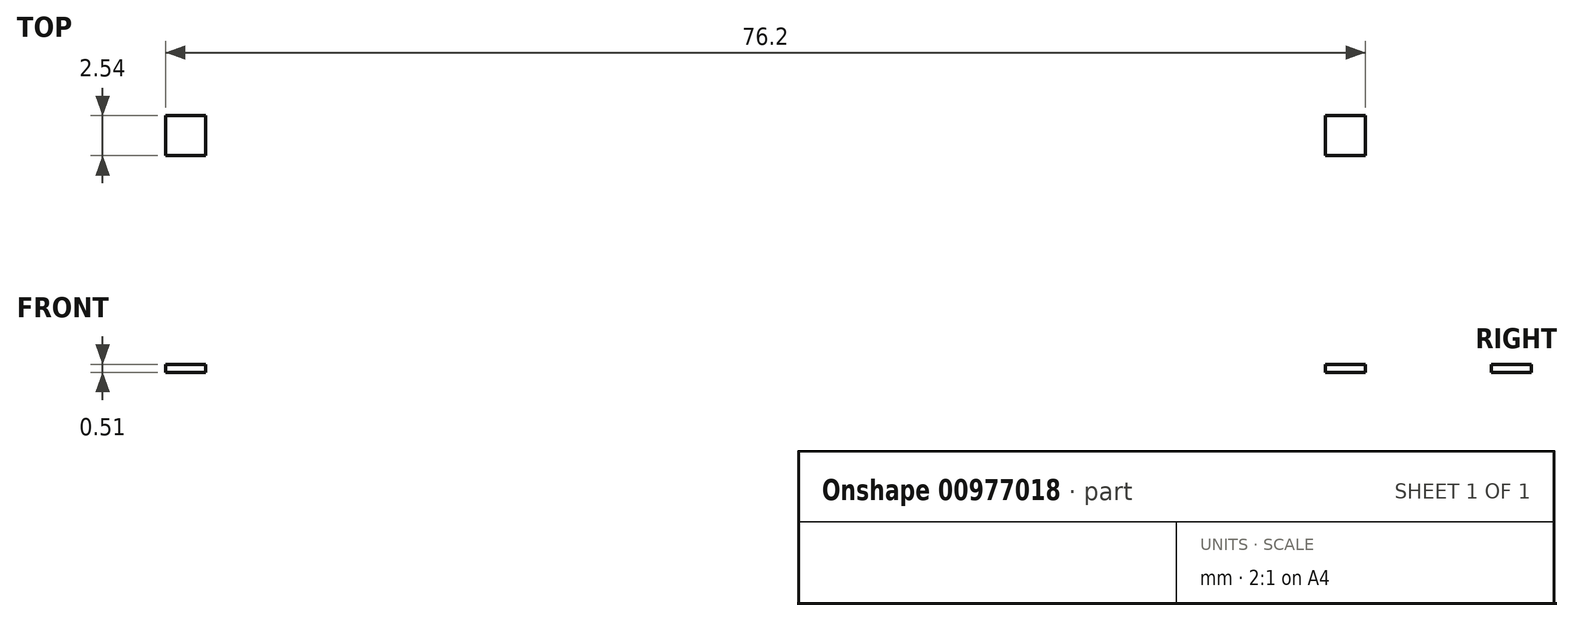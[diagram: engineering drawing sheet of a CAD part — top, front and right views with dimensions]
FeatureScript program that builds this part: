
annotation { "Feature Type Name" : "Feature", "Feature Type Description" : "" }
export const myFeature = defineFeature(function(context is Context, id is Id, definition is map)
    precondition{}
    {
        {
            var Q0;
            Q0=qCreatedBy(makeId("Top.planeOp"),FACE);
            var sketch = newSketch(context, id + "F0", { "sketchPlane" : qUnion([Q0])});
            skLineSegment(sketch, "E0.bottom", {"start": v(0, 0) * mm, "end": v(76.2, 0) * mm});
            skLineSegment(sketch, "E0.top", {"start": v(0, 59.18) * mm, "end": v(76.2, 59.18) * mm});
            skLineSegment(sketch, "E0.left", {"start": v(0, 0) * mm, "end": v(0, 59.18) * mm});
            skLineSegment(sketch, "E0.right", {"start": v(76.2, 0) * mm, "end": v(76.2, 59.18) * mm});
            skLineSegment(sketch, "E1.bottom", {"start": v(0, 59.18) * mm, "end": v(2.54, 59.18) * mm});
            skLineSegment(sketch, "E1.top", {"start": v(0, 56.64) * mm, "end": v(2.54, 56.64) * mm});
            skLineSegment(sketch, "E1.left", {"start": v(0, 59.18) * mm, "end": v(0, 56.64) * mm});
            skLineSegment(sketch, "E1.right", {"start": v(2.54, 59.18) * mm, "end": v(2.54, 56.64) * mm});
            skLineSegment(sketch, "E2.bottom", {"start": v(76.2, 59.18) * mm, "end": v(73.66, 59.18) * mm});
            skLineSegment(sketch, "E2.top", {"start": v(76.2, 56.64) * mm, "end": v(73.66, 56.64) * mm});
            skLineSegment(sketch, "E2.left", {"start": v(76.2, 59.18) * mm, "end": v(76.2, 56.64) * mm});
            skLineSegment(sketch, "E2.right", {"start": v(73.66, 59.18) * mm, "end": v(73.66, 56.64) * mm});
            skLineSegment(sketch, "E3.bottom", {"start": v(76.2, 0) * mm, "end": v(73.66, 0) * mm});
            skLineSegment(sketch, "E3.top", {"start": v(76.2, 2.54) * mm, "end": v(73.66, 2.54) * mm});
            skLineSegment(sketch, "E3.left", {"start": v(76.2, 0) * mm, "end": v(76.2, 2.54) * mm});
            skLineSegment(sketch, "E3.right", {"start": v(73.66, 0) * mm, "end": v(73.66, 2.54) * mm});
            skLineSegment(sketch, "E4.bottom", {"start": v(0, 0) * mm, "end": v(2.54, 0) * mm});
            skLineSegment(sketch, "E4.top", {"start": v(0, 2.54) * mm, "end": v(2.54, 2.54) * mm});
            skLineSegment(sketch, "E4.left", {"start": v(0, 0) * mm, "end": v(0, 2.54) * mm});
            skLineSegment(sketch, "E4.right", {"start": v(2.54, 0) * mm, "end": v(2.54, 2.54) * mm});
            skLineSegment(sketch, "E5", {"start": v(1.27, 2.54) * mm, "end": v(1.27, 6.75) * mm});
            skLineSegment(sketch, "E6", {"start": v(1.27, 2.54) * mm, "end": v(1.27, 4.65) * mm});
            skLineSegment(sketch, "E7", {"start": v(2.54, 1.27) * mm, "end": v(6.68, 1.27) * mm});
            skLineSegment(sketch, "E8", {"start": v(6.68, 1.27) * mm, "end": v(4.6, 1.27) * mm});
            skLineSegment(sketch, "E9", {"start": v(2.54, 57.91) * mm, "end": v(6.75, 57.91) * mm});
            skLineSegment(sketch, "E10", {"start": v(6.75, 57.91) * mm, "end": v(4.64, 57.91) * mm});
            skLineSegment(sketch, "E11", {"start": v(1.27, 56.64) * mm, "end": v(1.27, 52.42) * mm});
            skLineSegment(sketch, "E12", {"start": v(1.27, 52.42) * mm, "end": v(1.27, 54.53) * mm});
            skLineSegment(sketch, "E13", {"start": v(73.66, 57.91) * mm, "end": v(69.44, 57.91) * mm});
            skLineSegment(sketch, "E14", {"start": v(69.44, 57.91) * mm, "end": v(71.55, 57.91) * mm});
            skLineSegment(sketch, "E15", {"start": v(74.93, 56.64) * mm, "end": v(74.93, 52.43) * mm});
            skLineSegment(sketch, "E16", {"start": v(74.93, 52.43) * mm, "end": v(74.93, 54.54) * mm});
            skLineSegment(sketch, "E17", {"start": v(74.93, 2.54) * mm, "end": v(74.93, 6.76) * mm});
            skLineSegment(sketch, "E18", {"start": v(74.93, 6.76) * mm, "end": v(74.93, 4.65) * mm});
            skLineSegment(sketch, "E19", {"start": v(73.66, 1.27) * mm, "end": v(69.44, 1.27) * mm});
            skLineSegment(sketch, "E20", {"start": v(69.44, 1.27) * mm, "end": v(71.55, 1.27) * mm});
            skCircle(sketch, "E21", {"center": v(71.55, 1.27) * mm, "radius": 0.5 * mm});
            skCircle(sketch, "E22", {"center": v(69.44, 1.27) * mm, "radius": 0.52 * mm});
            skCircle(sketch, "E23", {"center": v(74.93, 4.65) * mm, "radius": 0.52 * mm});
            skCircle(sketch, "E24", {"center": v(74.93, 6.76) * mm, "radius": 0.5 * mm});
            skCircle(sketch, "E25", {"center": v(69.44, 57.91) * mm, "radius": 0.52 * mm});
            skCircle(sketch, "E26", {"center": v(71.55, 57.91) * mm, "radius": 0.5 * mm});
            skCircle(sketch, "E27", {"center": v(74.93, 54.54) * mm, "radius": 0.52 * mm});
            skCircle(sketch, "E28", {"center": v(74.93, 52.43) * mm, "radius": 0.5 * mm});
            skCircle(sketch, "E29", {"center": v(6.75, 57.91) * mm, "radius": 0.51 * mm});
            skCircle(sketch, "E30", {"center": v(4.64, 57.91) * mm, "radius": 0.51 * mm});
            skCircle(sketch, "E31", {"center": v(1.27, 54.53) * mm, "radius": 0.5 * mm});
            skCircle(sketch, "E32", {"center": v(1.27, 52.42) * mm, "radius": 0.5 * mm});
            skCircle(sketch, "E33", {"center": v(1.27, 6.75) * mm, "radius": 0.5 * mm});
            skCircle(sketch, "E34", {"center": v(1.27, 4.65) * mm, "radius": 0.5 * mm});
            skCircle(sketch, "E35", {"center": v(4.6, 1.27) * mm, "radius": 0.51 * mm});
            skCircle(sketch, "E36", {"center": v(6.68, 1.27) * mm, "radius": 0.5 * mm});
            skSolve(sketch);
        }
        {
            var Q0;
            {var subQ11=sQuery(id+"F0.wireOp",EDGE,"E0.bottom");Q0=makeQuery(id+"F0.imprint","IMPRINT",FACE,{"disambiguationData":[TD([[makeQuery(id+"F0.imprint","IMPRINT",EDGE,{"derivedFrom":subQ11}),1.0]])]});}
            extrude(context, id + "F1", {"entities" : qUnion([Q0]), "depth" : 0.5 * mm, "offsetDistance" : 25.4 * mm});
        }
    });
